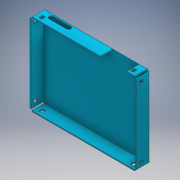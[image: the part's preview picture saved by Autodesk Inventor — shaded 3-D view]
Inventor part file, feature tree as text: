
AUTODESK INVENTOR PART (.ipt)
format: ipt  version: 2018 (Build 220112000, 112)  size: 264,704 bytes
history: native  units: mm
features: extrude x5, sketch x5, fillet x1
ambient origin geometry x8: Origin, YZ Plane, XZ Plane, XY Plane, X Axis, Y Axis, Z Axis, Center Point
bodies: Body1 (feature_tree)
feature tree (11):
  extrude  "Extrusion3"  Depth=2.0mm
  extrude  "Extrusion5"  Depth=2.0mm
  extrude  "Extrusion6"  Depth=0.5mm
  extrude  "Extrusion7"  Depth=0.5mm
  extrude  "Extrusion9"  Depth=0.5mm TaperAngle=0.0deg
  fillet  "Fillet1"  Radius=1.4mm
  sketch  "Sketch3"  dims[d21=2.0mm d22=2.0mm]
  sketch  "Sketch6"  dims[d23=2.0mm d24=2.0mm]
  sketch  "Sketch7"  dims[d31=0.5mm d32=0.0mm d45=0.5mm]
  sketch  "Sketch8"  dims[d46=0.5mm d48=2.0mm]
  sketch  "Sketch10"  dims[d49=0.5mm d50=5.5mm d51=0.0mm d52=1.4mm d53=1.7mm d54=3.1mm d55=1.7mm d56=1.4mm d57=1.7mm d58=3.1mm d59=1.7mm d60=5.5mm d61=0.0mm d62=1.4mm d63=1.7mm d64=3.1mm d65=1.2mm d66=1.4mm d67=1.7mm d68=3.1mm d69=1.2mm d70=5.5mm d71=0.0mm d80=12.0mm d81=5.5mm d82=0.5mm d83=3.5mm d84=9.9mm d85=2.0mm d87=3.5mm d88=1.0mm d89=1.0mm d90=1.0mm d91=10.0mm d92=0.0mm d93=0.5mm d94=3.0mm]
